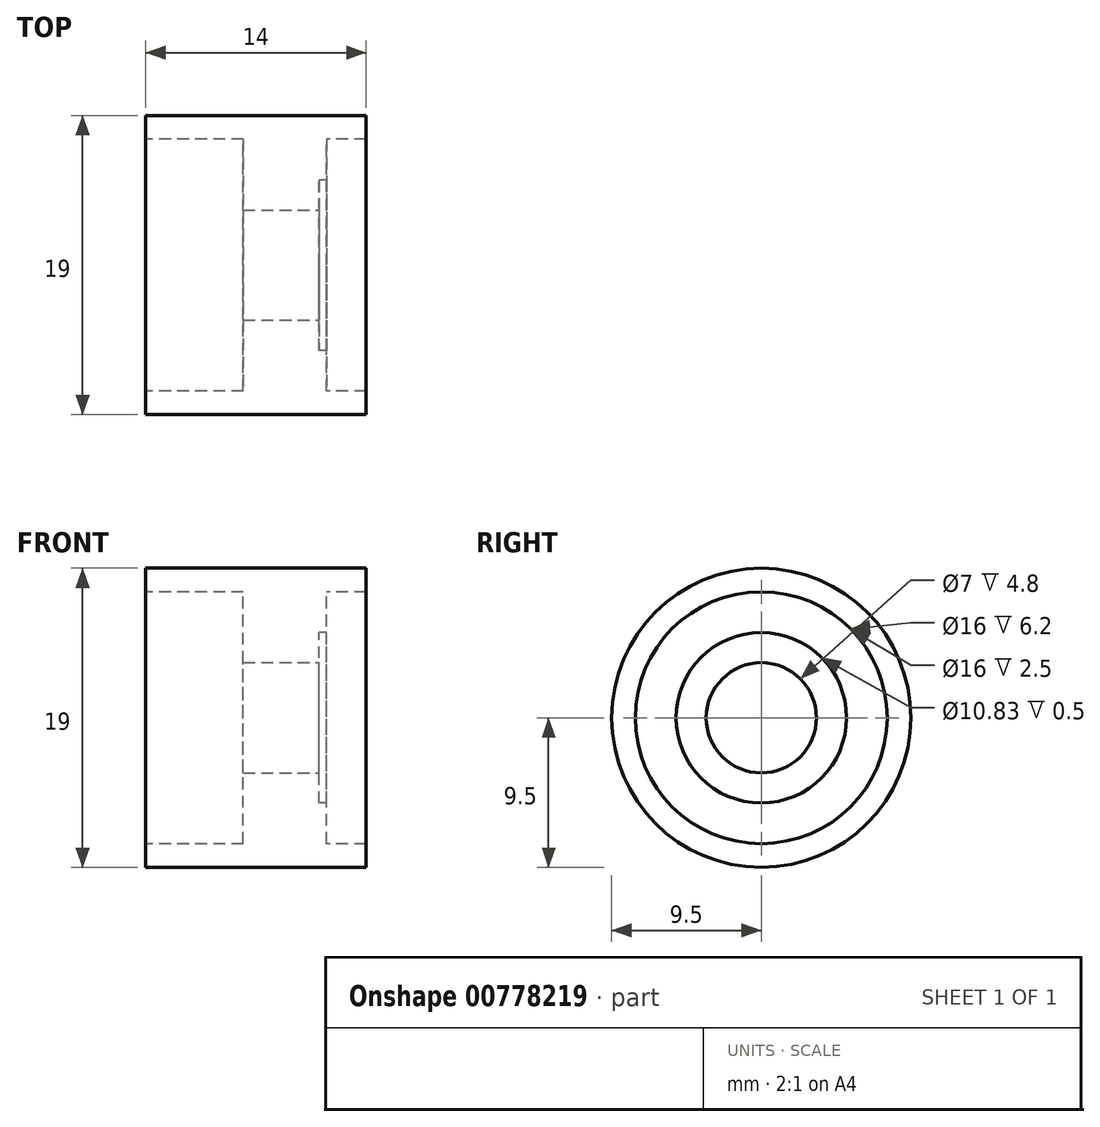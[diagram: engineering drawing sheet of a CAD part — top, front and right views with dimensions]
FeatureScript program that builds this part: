
annotation { "Feature Type Name" : "Feature", "Feature Type Description" : "" }
export const myFeature = defineFeature(function(context is Context, id is Id, definition is map)
    precondition{}
    {
        {
            var Q0;
            Q0=qCreatedBy(makeId("Right.planeOp"),FACE);
            var sketch = newSketch(context, id + "F0", { "sketchPlane" : qUnion([Q0])});
            skCircle(sketch, "E0", {"center": v(0, 0) * mm, "radius": 8 * mm});
            skCircle(sketch, "E1", {"center": v(0, 0) * mm, "radius": 9.5 * mm});
            skSolve(sketch);
        }
        {
            var Q0;
            Q0=makeQuery(id+"F0.imprint","IMPRINT",FACE,{"disambiguationData":[TD([[makeQuery(id+"F0.imprint","IMPRINT",EDGE,{"derivedFrom":sQuery(id+"F0.wireOp",EDGE,"E0")}),1.0]])]});
            extrude(context, id + "F1", {"entities" : qUnion([Q0]), "depth" : 14 * mm, "offsetDistance" : 25 * mm});
        }
        {
            var Q0;
            Q0=makeQuery(id+"F1.opExtrude","CAP_FACE",FACE,{"disambiguationData":[OSD([sQuery(id+"F0.wireOp",EDGE,"E0")])],"isStart":true});
            var sketch = newSketch(context, id + "F2", { "sketchPlane" : qUnion([Q0])});
            skCircle(sketch, "E2", {"center": v(0, 0) * mm, "radius": 9.5 * mm});
            skSolve(sketch);
        }
        {
            var Q0;
            Q0=makeQuery(id+"F2.imprint","IMPRINT",FACE,{"disambiguationData":[TD([[makeQuery(id+"F2.imprint","IMPRINT",EDGE,{"derivedFrom":sQuery(id+"F2.wireOp",EDGE,"E2")}),1.0]])]});
            extrude(context, id + "F3", {"entities" : qUnion([Q0]), "oppositeDirection" : true, "depth" : 14 * mm, "offsetDistance" : 25 * mm});
        }
        {
            var Q0;
            Q0=makeQuery(id+"F1.opExtrude","CAP_FACE",FACE,{"disambiguationData":[OSD([sQuery(id+"F0.wireOp",EDGE,"E0")])],"isStart":false});
            extrude(context, id + "F4", {"entities" : qUnion([Q0]), "operationType" : NewBodyOperationType.REMOVE, "oppositeDirection" : true, "depth" : 3 * mm, "offsetDistance" : 25 * mm});
        }
        {
            var Q0;
            Q0=makeQuery(id+"F1.opExtrude","CAP_FACE",FACE,{"disambiguationData":[OSD([sQuery(id+"F0.wireOp",EDGE,"E0")])],"isStart":true});
            extrude(context, id + "F5", {"entities" : qUnion([Q0]), "operationType" : NewBodyOperationType.REMOVE, "oppositeDirection" : true, "depth" : 6.2 * mm, "offsetDistance" : 25 * mm});
        }
        {
            var Q0;
            Q0=makeQuery(id+"F4.boolean.opBoolean","COPY",FACE,{"derivedFrom":makeQuery(id+"F4.opExtrude","CAP_FACE",FACE,{"disambiguationData":[OSD([sQuery(id+"F0.wireOp",EDGE,"E0")])],"isStart":false})});
            var sketch = newSketch(context, id + "F6", { "sketchPlane" : qUnion([Q0])});
            skCircle(sketch, "E3", {"center": v(0, 0) * mm, "radius": 3.5 * mm});
            skSolve(sketch);
        }
        {
            var Q0;
            Q0=makeQuery(id+"F6.imprint","IMPRINT",FACE,{"disambiguationData":[TD([[makeQuery(id+"F6.imprint","IMPRINT",EDGE,{"derivedFrom":sQuery(id+"F6.wireOp",EDGE,"E3")}),1.0]])]});
            extrude(context, id + "F7", {"entities" : qUnion([Q0]), "operationType" : NewBodyOperationType.REMOVE, "endBound" : BoundingType.THROUGH_ALL, "oppositeDirection" : true, "depth" : 25 * mm, "offsetDistance" : 25 * mm});
        }
        {
            var Q0;
            Q0=makeQuery(id+"F4.boolean.opBoolean","COPY",FACE,{"derivedFrom":makeQuery(id+"F4.opExtrude","CAP_FACE",FACE,{"disambiguationData":[OSD([sQuery(id+"F0.wireOp",EDGE,"E0")])],"isStart":false})});
            var sketch = newSketch(context, id + "F8", { "sketchPlane" : qUnion([Q0])});
            skLineSegment(sketch, "E4", {"start": v(0, 0) * mm, "end": v(0, 8) * mm, "construction": true});
            skCircle(sketch, "E5", {"center": v(0, 0) * mm, "radius": 4 * mm, "construction": true});
            skLineSegment(sketch, "E6", {"start": v(0, 4) * mm, "end": v(0.48, 7.99) * mm});
            skCircle(sketch, "E7", {"center": v(0, 0) * mm, "radius": 8 * mm});
            skLineSegment(sketch, "E8.MirrorCS", {"start": v(0, 4) * mm, "end": v(-0.48, 7.99) * mm});
            skLineSegment(sketch, "E9.1.0", {"start": v(-2.83, 2.83) * mm, "end": v(-5.3, 5.99) * mm});
            skLineSegment(sketch, "E9.1.1", {"start": v(-2.83, 2.83) * mm, "end": v(-5.99, 5.3) * mm});
            skLineSegment(sketch, "E9.2.0", {"start": v(-4, 0) * mm, "end": v(-7.99, 0.48) * mm});
            skLineSegment(sketch, "E9.2.1", {"start": v(-4, 0) * mm, "end": v(-7.99, -0.48) * mm});
            skLineSegment(sketch, "E9.3.0", {"start": v(-2.83, -2.83) * mm, "end": v(-5.99, -5.3) * mm});
            skLineSegment(sketch, "E9.3.1", {"start": v(-2.83, -2.83) * mm, "end": v(-5.3, -5.99) * mm});
            skLineSegment(sketch, "E9.4.0", {"start": v(0, -4) * mm, "end": v(-0.48, -7.99) * mm});
            skLineSegment(sketch, "E9.4.1", {"start": v(0, -4) * mm, "end": v(0.48, -7.99) * mm});
            skLineSegment(sketch, "E9.5.0", {"start": v(2.83, -2.83) * mm, "end": v(5.3, -5.99) * mm});
            skLineSegment(sketch, "E9.5.1", {"start": v(2.83, -2.83) * mm, "end": v(5.99, -5.3) * mm});
            skLineSegment(sketch, "E9.6.0", {"start": v(4, 0) * mm, "end": v(7.99, -0.48) * mm});
            skLineSegment(sketch, "E9.6.1", {"start": v(4, 0) * mm, "end": v(7.99, 0.48) * mm});
            skLineSegment(sketch, "E9.7.0", {"start": v(2.83, 2.83) * mm, "end": v(5.99, 5.3) * mm});
            skLineSegment(sketch, "E9.7.1", {"start": v(2.83, 2.83) * mm, "end": v(5.3, 5.99) * mm});
            skLineSegment(sketch, "E10", {"start": v(0, 0) * mm, "end": v(3.06, 7.4) * mm, "construction": true});
            skPoint(sketch, "E11.end.orphan", {"position": v(3.56, 7.17) * mm});
            skPoint(sketch, "E12.start.orphan", {"position": v(1.53, 3.7) * mm});
            skLineSegment(sketch, "E13", {"start": v(0, 0) * mm, "end": v(2.83, 2.83) * mm, "construction": true});
            skLineSegment(sketch, "E14", {"start": v(1.53, 3.7) * mm, "end": v(3.5, 7.2) * mm});
            skLineSegment(sketch, "E15.MirrorCS", {"start": v(1.53, 3.7) * mm, "end": v(2.61, 7.56) * mm});
            skLineSegment(sketch, "E16.1.0", {"start": v(-1.53, 3.7) * mm, "end": v(-2.61, 7.56) * mm});
            skLineSegment(sketch, "E16.1.1", {"start": v(-1.53, 3.7) * mm, "end": v(-3.5, 7.2) * mm});
            skLineSegment(sketch, "E16.2.0", {"start": v(-3.7, 1.53) * mm, "end": v(-7.2, 3.5) * mm});
            skLineSegment(sketch, "E16.2.1", {"start": v(-3.7, 1.53) * mm, "end": v(-7.56, 2.61) * mm});
            skLineSegment(sketch, "E16.3.0", {"start": v(-3.7, -1.53) * mm, "end": v(-7.56, -2.61) * mm});
            skLineSegment(sketch, "E16.3.1", {"start": v(-3.7, -1.53) * mm, "end": v(-7.2, -3.5) * mm});
            skLineSegment(sketch, "E16.4.0", {"start": v(-1.53, -3.7) * mm, "end": v(-3.5, -7.2) * mm});
            skLineSegment(sketch, "E16.4.1", {"start": v(-1.53, -3.7) * mm, "end": v(-2.61, -7.56) * mm});
            skLineSegment(sketch, "E16.5.0", {"start": v(1.53, -3.7) * mm, "end": v(2.61, -7.56) * mm});
            skLineSegment(sketch, "E16.5.1", {"start": v(1.53, -3.7) * mm, "end": v(3.5, -7.2) * mm});
            skLineSegment(sketch, "E16.6.0", {"start": v(3.7, -1.53) * mm, "end": v(7.2, -3.5) * mm});
            skLineSegment(sketch, "E16.6.1", {"start": v(3.7, -1.53) * mm, "end": v(7.56, -2.61) * mm});
            skLineSegment(sketch, "E16.7.0", {"start": v(3.7, 1.53) * mm, "end": v(7.56, 2.61) * mm});
            skLineSegment(sketch, "E16.7.1", {"start": v(3.7, 1.53) * mm, "end": v(7.2, 3.5) * mm});
            skCircle(sketch, "E17", {"center": v(0, 0) * mm, "radius": 5.41 * mm});
            skSolve(sketch);
        }
        {
            var Q0;
            {var subQ0=sQuery(id+"F8.wireOp",EDGE,"E9.3.0");var subQ1=sQuery(id+"F8.wireOp",EDGE,"E7");var subQ2=makeQuery(id+"F8.imprint","INTERSECT",VERTEX,{"derivedFrom":[subQ1,subQ0]});Q0=makeQuery(id+"F8.imprint","IMPRINT",FACE,{"disambiguationData":[TD([[makeQuery(id+"F8.imprint","IMPRINT",EDGE,{"disambiguationData":[TD([[subQ2,-1.0]])],"derivedFrom":subQ1}),1.0]])]});}
            var Q1;
            {var subQ0=sQuery(id+"F8.wireOp",EDGE,"E16.3.0");var subQ1=sQuery(id+"F8.wireOp",EDGE,"E7");var subQ2=makeQuery(id+"F8.imprint","INTERSECT",VERTEX,{"derivedFrom":[subQ1,subQ0]});Q1=makeQuery(id+"F8.imprint","IMPRINT",FACE,{"disambiguationData":[TD([[makeQuery(id+"F8.imprint","IMPRINT",EDGE,{"disambiguationData":[TD([[subQ2,-1.0]])],"derivedFrom":subQ1}),1.0]])]});}
            var Q2;
            {var subQ0=sQuery(id+"F8.wireOp",EDGE,"E9.2.0");var subQ1=sQuery(id+"F8.wireOp",EDGE,"E7");var subQ2=makeQuery(id+"F8.imprint","INTERSECT",VERTEX,{"derivedFrom":[subQ1,subQ0]});Q2=makeQuery(id+"F8.imprint","IMPRINT",FACE,{"disambiguationData":[TD([[makeQuery(id+"F8.imprint","IMPRINT",EDGE,{"disambiguationData":[TD([[subQ2,-1.0]])],"derivedFrom":subQ1}),1.0]])]});}
            var Q3;
            {var subQ0=sQuery(id+"F8.wireOp",EDGE,"E16.2.0");var subQ1=sQuery(id+"F8.wireOp",EDGE,"E7");var subQ2=makeQuery(id+"F8.imprint","INTERSECT",VERTEX,{"derivedFrom":[subQ1,subQ0]});Q3=makeQuery(id+"F8.imprint","IMPRINT",FACE,{"disambiguationData":[TD([[makeQuery(id+"F8.imprint","IMPRINT",EDGE,{"disambiguationData":[TD([[subQ2,-1.0]])],"derivedFrom":subQ1}),1.0]])]});}
            var Q4;
            {var subQ0=sQuery(id+"F8.wireOp",EDGE,"E9.1.0");var subQ1=sQuery(id+"F8.wireOp",EDGE,"E7");var subQ2=makeQuery(id+"F8.imprint","INTERSECT",VERTEX,{"derivedFrom":[subQ1,subQ0]});Q4=makeQuery(id+"F8.imprint","IMPRINT",FACE,{"disambiguationData":[TD([[makeQuery(id+"F8.imprint","IMPRINT",EDGE,{"disambiguationData":[TD([[subQ2,-1.0]])],"derivedFrom":subQ1}),1.0]])]});}
            var Q5;
            {var subQ0=sQuery(id+"F8.wireOp",EDGE,"E16.1.0");var subQ1=sQuery(id+"F8.wireOp",EDGE,"E7");var subQ2=makeQuery(id+"F8.imprint","INTERSECT",VERTEX,{"derivedFrom":[subQ1,subQ0]});Q5=makeQuery(id+"F8.imprint","IMPRINT",FACE,{"disambiguationData":[TD([[makeQuery(id+"F8.imprint","IMPRINT",EDGE,{"disambiguationData":[TD([[subQ2,-1.0]])],"derivedFrom":subQ1}),1.0]])]});}
            var Q6;
            {var subQ0=sQuery(id+"F8.wireOp",EDGE,"E7");var subQ1=sQuery(id+"F8.wireOp",EDGE,"E6");var subQ2=makeQuery(id+"F8.imprint","INTERSECT",VERTEX,{"derivedFrom":[subQ1,subQ0]});Q6=makeQuery(id+"F8.imprint","IMPRINT",FACE,{"disambiguationData":[TD([[makeQuery(id+"F8.imprint","IMPRINT",EDGE,{"disambiguationData":[TD([[subQ2,1.0]])],"derivedFrom":subQ1}),1.0]])]});}
            var Q7;
            {var subQ0=sQuery(id+"F8.wireOp",EDGE,"E14");var subQ1=sQuery(id+"F8.wireOp",EDGE,"E7");var subQ2=makeQuery(id+"F8.imprint","INTERSECT",VERTEX,{"derivedFrom":[subQ1,subQ0]});Q7=makeQuery(id+"F8.imprint","IMPRINT",FACE,{"disambiguationData":[TD([[makeQuery(id+"F8.imprint","IMPRINT",EDGE,{"disambiguationData":[TD([[subQ2,-1.0]])],"derivedFrom":subQ1}),1.0]])]});}
            var Q8;
            {var subQ0=sQuery(id+"F8.wireOp",EDGE,"E9.7.1");var subQ1=sQuery(id+"F8.wireOp",EDGE,"E7");var subQ2=makeQuery(id+"F8.imprint","INTERSECT",VERTEX,{"derivedFrom":[subQ1,subQ0]});Q8=makeQuery(id+"F8.imprint","IMPRINT",FACE,{"disambiguationData":[TD([[makeQuery(id+"F8.imprint","IMPRINT",EDGE,{"disambiguationData":[TD([[subQ2,1.0]])],"derivedFrom":subQ1}),1.0]])]});}
            var Q9;
            {var subQ0=sQuery(id+"F8.wireOp",EDGE,"E16.7.0");var subQ1=sQuery(id+"F8.wireOp",EDGE,"E7");var subQ2=makeQuery(id+"F8.imprint","INTERSECT",VERTEX,{"derivedFrom":[subQ1,subQ0]});Q9=makeQuery(id+"F8.imprint","IMPRINT",FACE,{"disambiguationData":[TD([[makeQuery(id+"F8.imprint","IMPRINT",EDGE,{"disambiguationData":[TD([[subQ2,-1.0]])],"derivedFrom":subQ1}),1.0]])]});}
            var Q10;
            {var subQ0=sQuery(id+"F8.wireOp",EDGE,"E9.6.0");var subQ1=sQuery(id+"F8.wireOp",EDGE,"E7");var subQ2=makeQuery(id+"F8.imprint","INTERSECT",VERTEX,{"derivedFrom":[subQ1,subQ0]});Q10=makeQuery(id+"F8.imprint","IMPRINT",FACE,{"disambiguationData":[TD([[makeQuery(id+"F8.imprint","IMPRINT",EDGE,{"disambiguationData":[TD([[subQ2,-1.0]])],"derivedFrom":subQ1}),1.0]])]});}
            var Q11;
            {var subQ0=sQuery(id+"F8.wireOp",EDGE,"E16.6.0");var subQ1=sQuery(id+"F8.wireOp",EDGE,"E7");var subQ2=makeQuery(id+"F8.imprint","INTERSECT",VERTEX,{"derivedFrom":[subQ1,subQ0]});Q11=makeQuery(id+"F8.imprint","IMPRINT",FACE,{"disambiguationData":[TD([[makeQuery(id+"F8.imprint","IMPRINT",EDGE,{"disambiguationData":[TD([[subQ2,-1.0]])],"derivedFrom":subQ1}),1.0]])]});}
            var Q12;
            {var subQ0=sQuery(id+"F8.wireOp",EDGE,"E9.5.0");var subQ1=sQuery(id+"F8.wireOp",EDGE,"E7");var subQ2=makeQuery(id+"F8.imprint","INTERSECT",VERTEX,{"derivedFrom":[subQ1,subQ0]});Q12=makeQuery(id+"F8.imprint","IMPRINT",FACE,{"disambiguationData":[TD([[makeQuery(id+"F8.imprint","IMPRINT",EDGE,{"disambiguationData":[TD([[subQ2,-1.0]])],"derivedFrom":subQ1}),1.0]])]});}
            var Q13;
            {var subQ0=sQuery(id+"F8.wireOp",EDGE,"E16.5.0");var subQ1=sQuery(id+"F8.wireOp",EDGE,"E7");var subQ2=makeQuery(id+"F8.imprint","INTERSECT",VERTEX,{"derivedFrom":[subQ1,subQ0]});Q13=makeQuery(id+"F8.imprint","IMPRINT",FACE,{"disambiguationData":[TD([[makeQuery(id+"F8.imprint","IMPRINT",EDGE,{"disambiguationData":[TD([[subQ2,-1.0]])],"derivedFrom":subQ1}),1.0]])]});}
            var Q14;
            {var subQ0=sQuery(id+"F8.wireOp",EDGE,"E9.4.0");var subQ1=sQuery(id+"F8.wireOp",EDGE,"E7");var subQ2=makeQuery(id+"F8.imprint","INTERSECT",VERTEX,{"derivedFrom":[subQ1,subQ0]});Q14=makeQuery(id+"F8.imprint","IMPRINT",FACE,{"disambiguationData":[TD([[makeQuery(id+"F8.imprint","IMPRINT",EDGE,{"disambiguationData":[TD([[subQ2,-1.0]])],"derivedFrom":subQ1}),1.0]])]});}
            var Q15;
            {var subQ0=sQuery(id+"F8.wireOp",EDGE,"E16.4.0");var subQ1=sQuery(id+"F8.wireOp",EDGE,"E7");var subQ2=makeQuery(id+"F8.imprint","INTERSECT",VERTEX,{"derivedFrom":[subQ1,subQ0]});Q15=makeQuery(id+"F8.imprint","IMPRINT",FACE,{"disambiguationData":[TD([[makeQuery(id+"F8.imprint","IMPRINT",EDGE,{"disambiguationData":[TD([[subQ2,-1.0]])],"derivedFrom":subQ1}),1.0]])]});}
            extrude(context, id + "F9", {"entities" : qUnion([Q0, Q1, Q2, Q3, Q4, Q5, Q6, Q7, Q8, Q9, Q10, Q11, Q12, Q13, Q14, Q15]), "operationType" : NewBodyOperationType.ADD, "depth" : .5 * mm, "offsetDistance" : 25 * mm});
        }
    });
